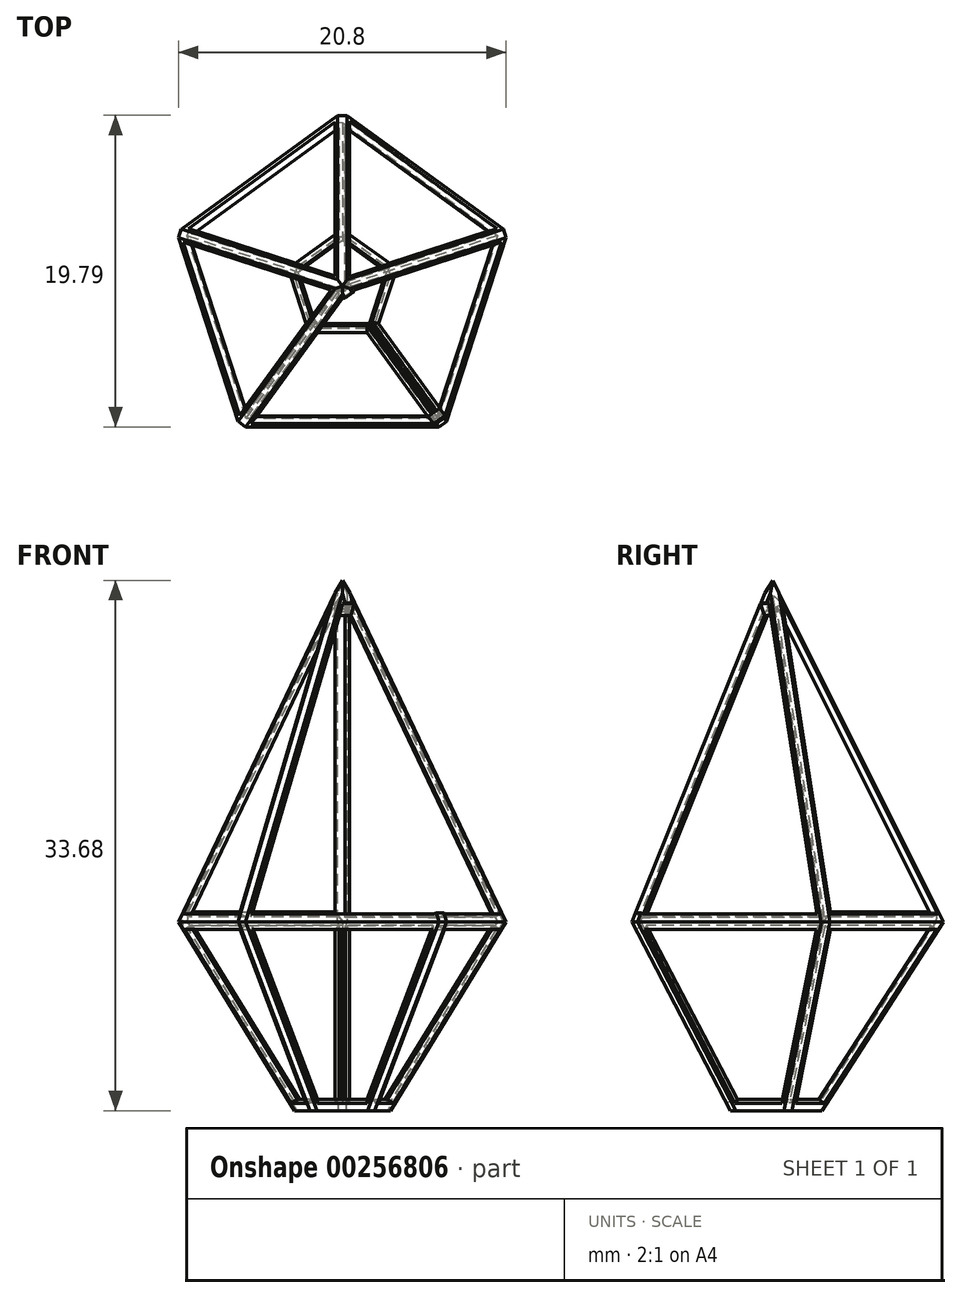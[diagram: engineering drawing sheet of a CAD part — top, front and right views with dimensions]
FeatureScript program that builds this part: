
annotation { "Feature Type Name" : "Feature", "Feature Type Description" : "" }
export const myFeature = defineFeature(function(context is Context, id is Id, definition is map)
    precondition{}
    {
        {
            var Q0;
            Q0=qCreatedBy(makeId("Top.planeOp"),FACE);
            var sketch = newSketch(context, id + "F0", { "sketchPlane" : qUnion([Q0])});
            skCircle(sketch, "E0.cCircle", {"center": v(0, 0) * mm, "radius": 8.94 * mm, "construction": true});
            skLineSegment(sketch, "E0.0", {"start": v(6.5, -8.94) * mm, "end": v(-6.5, -8.94) * mm});
            skLineSegment(sketch, "E0.1", {"start": v(-6.5, -8.94) * mm, "end": v(-10.51, 3.42) * mm});
            skLineSegment(sketch, "E0.2", {"start": v(-10.51, 3.42) * mm, "end": v(0, 11.06) * mm});
            skLineSegment(sketch, "E0.3", {"start": v(0, 11.06) * mm, "end": v(10.51, 3.42) * mm});
            skLineSegment(sketch, "E0.4", {"start": v(10.51, 3.42) * mm, "end": v(6.5, -8.94) * mm});
            skPoint(sketch, "E0.0.midPoint", {"position": v(0, -8.94) * mm});
            skSolve(sketch);
        }
        {
            var Q0;
            Q0=qCreatedBy(makeId("Top.planeOp"),FACE);
            cPlane(context, id + "F1", {"entities" : qUnion([Q0]), "cplaneType" : CPlaneType.OFFSET, "offset" : 22 * mm, "width" : 152.4 * mm, "height" : 152.4 * mm});
        }
        {
            var Q0;
            Q0=qCreatedBy(id+"F1.planeOp",FACE);
            var sketch = newSketch(context, id + "F2", { "sketchPlane" : qUnion([Q0])});
            skCircle(sketch, "E1.cCircle", {"center": v(0, 0) * mm, "radius": 0.04 * mm, "construction": true});
            skLineSegment(sketch, "E1.0", {"start": v(0.03, -0.04) * mm, "end": v(-0.03, -0.04) * mm});
            skLineSegment(sketch, "E1.1", {"start": v(-0.03, -0.04) * mm, "end": v(-0.05, 0.02) * mm});
            skLineSegment(sketch, "E1.2", {"start": v(-0.05, 0.02) * mm, "end": v(0, 0.06) * mm});
            skLineSegment(sketch, "E1.3", {"start": v(0, 0.06) * mm, "end": v(0.05, 0.02) * mm});
            skLineSegment(sketch, "E1.4", {"start": v(0.05, 0.02) * mm, "end": v(0.03, -0.04) * mm});
            skPoint(sketch, "E1.0.midPoint", {"position": v(0, -0.04) * mm});
            skSolve(sketch);
        }
        {
            var Q0;
            Q0=makeQuery(id+"F0.imprint","IMPRINT",FACE,{"disambiguationData":[TD([[makeQuery(id+"F0.imprint","IMPRINT",EDGE,{"derivedFrom":sQuery(id+"F0.wireOp",EDGE,"E0.0")}),-1.0]])]});
            var Q1;
            Q1=makeQuery(id+"F2.imprint","IMPRINT",FACE,{"disambiguationData":[TD([[makeQuery(id+"F2.imprint","IMPRINT",EDGE,{"derivedFrom":sQuery(id+"F2.wireOp",EDGE,"E1.0")}),-1.0]])]});
            loft(context, id + "F3", {"sheetProfilesArray" : [{ "sheetProfileEntities" : qUnion([Q0]) }, { "sheetProfileEntities" : qUnion([Q1]) }]});
        }
        {
            var Q0;
            Q0=qCreatedBy(makeId("Top.planeOp"),FACE);
            cPlane(context, id + "F4", {"entities" : qUnion([Q0]), "cplaneType" : CPlaneType.OFFSET, "offset" : 12 * mm, "oppositeDirection" : true, "width" : 150 * mm, "height" : 150 * mm});
        }
        {
            var Q0;
            Q0=qCreatedBy(id+"F4.planeOp",FACE);
            var sketch = newSketch(context, id + "F5", { "sketchPlane" : qUnion([Q0])});
            skCircle(sketch, "E2.cCircle", {"center": v(0, 0) * mm, "radius": 2.68 * mm, "construction": true});
            skLineSegment(sketch, "E2.0", {"start": v(1.95, -2.68) * mm, "end": v(-1.95, -2.68) * mm});
            skLineSegment(sketch, "E2.1", {"start": v(-1.95, -2.68) * mm, "end": v(-3.15, 1.02) * mm});
            skLineSegment(sketch, "E2.2", {"start": v(-3.15, 1.02) * mm, "end": v(0, 3.32) * mm});
            skLineSegment(sketch, "E2.3", {"start": v(0, 3.32) * mm, "end": v(3.15, 1.02) * mm});
            skLineSegment(sketch, "E2.4", {"start": v(3.15, 1.02) * mm, "end": v(1.95, -2.68) * mm});
            skPoint(sketch, "E2.0.midPoint", {"position": v(0, -2.68) * mm});
            skSolve(sketch);
        }
        {
            var Q1;
            Q1=makeQuery(id+"F3.opLoft","CAP_FACE",FACE,{"disambiguationData":[OSD([makeQuery(id+"F0.imprint","IMPRINT",FACE,{"disambiguationData":[TD([[makeQuery(id+"F0.imprint","IMPRINT",EDGE,{"derivedFrom":sQuery(id+"F0.wireOp",EDGE,"E0.0")}),-1.0]])]})])],"isStart":true});
            var Q2;
            Q2=makeQuery(id+"F5.imprint","IMPRINT",FACE,{"disambiguationData":[TD([[makeQuery(id+"F5.imprint","IMPRINT",EDGE,{"derivedFrom":sQuery(id+"F5.wireOp",EDGE,"E2.0")}),-1.0]])]});
            loft(context, id + "F6", {"operationType" : NewBodyOperationType.ADD, "sheetProfilesArray" : [{ "sheetProfileEntities" : qUnion([Q1]) }, { "sheetProfileEntities" : qUnion([Q2]) }]});
        }
        {
            var Q0;
            Q0=makeQuery(id+"F3.opLoft","SWEPT_FACE",FACE,{"disambiguationData":[OSD([sQuery(id+"F0.wireOp",EDGE,"E0.1"),sQuery(id+"F0.wireOp",EDGE,"E0.2"),sQuery(id+"F0.wireOp",EDGE,"E0.3"),sQuery(id+"F2.wireOp",EDGE,"E1.1"),sQuery(id+"F2.wireOp",EDGE,"E1.2"),sQuery(id+"F2.wireOp",EDGE,"E1.3")])]});
            shell(context, id + "F7", {"entities" : qUnion([Q0]), "thickness" : .5 * mm});
        }
        {
            var Q0;
            Q0=makeQuery(id+"F3.opLoft","SWEPT_FACE",FACE,{"disambiguationData":[OSD([sQuery(id+"F0.wireOp",EDGE,"E0.0"),sQuery(id+"F0.wireOp",EDGE,"E0.1"),sQuery(id+"F0.wireOp",EDGE,"E0.2"),sQuery(id+"F2.wireOp",EDGE,"E1.0"),sQuery(id+"F2.wireOp",EDGE,"E1.1"),sQuery(id+"F2.wireOp",EDGE,"E1.2")])]});
            var sketch = newSketch(context, id + "F8", { "sketchPlane" : qUnion([Q0])});
            skLineSegment(sketch, "E3", {"start": v(-5.4, -3.5) * mm, "end": v(6.1, -2.1) * mm});
            skLineSegment(sketch, "E4", {"start": v(6.1, -2.1) * mm, "end": v(-2.23, 18.31) * mm});
            skLineSegment(sketch, "E5", {"start": v(-2.23, 18.31) * mm, "end": v(-5.4, -3.5) * mm});
            skSolve(sketch);
        }
        {
            var Q0;
            Q0=makeQuery(id+"F3.opLoft","SWEPT_FACE",FACE,{"disambiguationData":[OSD([sQuery(id+"F0.wireOp",EDGE,"E0.0"),sQuery(id+"F0.wireOp",EDGE,"E0.1"),sQuery(id+"F0.wireOp",EDGE,"E0.4"),sQuery(id+"F2.wireOp",EDGE,"E1.0"),sQuery(id+"F2.wireOp",EDGE,"E1.1"),sQuery(id+"F2.wireOp",EDGE,"E1.4")])]});
            var sketch = newSketch(context, id + "F9", { "sketchPlane" : qUnion([Q0])});
            skLineSegment(sketch, "E6", {"start": v(-5.8, -2.81) * mm, "end": v(5.8, -2.81) * mm});
            skLineSegment(sketch, "E7", {"start": v(5.8, -2.81) * mm, "end": v(0, 18.44) * mm});
            skLineSegment(sketch, "E8", {"start": v(0, 18.44) * mm, "end": v(-5.8, -2.81) * mm});
            skSolve(sketch);
        }
        {
            var Q0;
            Q0=makeQuery(id+"F3.opLoft","SWEPT_FACE",FACE,{"disambiguationData":[OSD([sQuery(id+"F0.wireOp",EDGE,"E0.0"),sQuery(id+"F0.wireOp",EDGE,"E0.3"),sQuery(id+"F0.wireOp",EDGE,"E0.4"),sQuery(id+"F2.wireOp",EDGE,"E1.0"),sQuery(id+"F2.wireOp",EDGE,"E1.3"),sQuery(id+"F2.wireOp",EDGE,"E1.4")])]});
            var sketch = newSketch(context, id + "F10", { "sketchPlane" : qUnion([Q0])});
            skLineSegment(sketch, "E9", {"start": v(-6.09, -2.1) * mm, "end": v(5.4, -3.5) * mm});
            skLineSegment(sketch, "E10", {"start": v(5.4, -3.5) * mm, "end": v(2.23, 18.3) * mm});
            skLineSegment(sketch, "E11", {"start": v(2.23, 18.3) * mm, "end": v(-6.09, -2.1) * mm});
            skSolve(sketch);
        }
        {
            var Q0;
            Q0=makeQuery(id+"F3.opLoft","SWEPT_FACE",FACE,{"disambiguationData":[OSD([sQuery(id+"F0.wireOp",EDGE,"E0.2"),sQuery(id+"F0.wireOp",EDGE,"E0.3"),sQuery(id+"F0.wireOp",EDGE,"E0.4"),sQuery(id+"F2.wireOp",EDGE,"E1.2"),sQuery(id+"F2.wireOp",EDGE,"E1.3"),sQuery(id+"F2.wireOp",EDGE,"E1.4")])]});
            var sketch = newSketch(context, id + "F11", { "sketchPlane" : qUnion([Q0])});
            skLineSegment(sketch, "E12", {"start": v(-6.33, -1.2) * mm, "end": v(4.85, -4.24) * mm});
            skLineSegment(sketch, "E13", {"start": v(4.85, -4.24) * mm, "end": v(4.85, 17.8) * mm});
            skLineSegment(sketch, "E14", {"start": v(4.85, 17.8) * mm, "end": v(-6.33, -1.2) * mm});
            skSolve(sketch);
        }
        {
            var Q0;
            Q0=makeQuery(id+"F11.imprint","IMPRINT",FACE,{"disambiguationData":[TD([[makeQuery(id+"F11.imprint","IMPRINT",EDGE,{"derivedFrom":sQuery(id+"F11.wireOp",EDGE,"E12")}),1.0]])]});
            extrude(context, id + "F12", {"entities" : qUnion([Q0]), "operationType" : NewBodyOperationType.REMOVE, "oppositeDirection" : true, "depth" : 1 * mm});
        }
        {
            var Q0;
            Q0=makeQuery(id+"F10.imprint","IMPRINT",FACE,{"disambiguationData":[TD([[makeQuery(id+"F10.imprint","IMPRINT",EDGE,{"derivedFrom":sQuery(id+"F10.wireOp",EDGE,"E9")}),1.0]])]});
            extrude(context, id + "F13", {"entities" : qUnion([Q0]), "operationType" : NewBodyOperationType.REMOVE, "oppositeDirection" : true, "depth" : 1 * mm});
        }
        {
            var Q0;
            Q0=makeQuery(id+"F8.imprint","IMPRINT",FACE,{"disambiguationData":[TD([[makeQuery(id+"F8.imprint","IMPRINT",EDGE,{"derivedFrom":sQuery(id+"F8.wireOp",EDGE,"E3")}),1.0]])]});
            extrude(context, id + "F14", {"entities" : qUnion([Q0]), "operationType" : NewBodyOperationType.REMOVE, "oppositeDirection" : true, "depth" : 1 * mm});
        }
        {
            var Q0;
            Q0=makeQuery(id+"F9.imprint","IMPRINT",FACE,{"disambiguationData":[TD([[makeQuery(id+"F9.imprint","IMPRINT",EDGE,{"derivedFrom":sQuery(id+"F9.wireOp",EDGE,"E6")}),1.0]])]});
            extrude(context, id + "F15", {"entities" : qUnion([Q0]), "operationType" : NewBodyOperationType.REMOVE, "oppositeDirection" : true, "depth" : 1 * mm});
        }
        {
            var Q0;
            Q0=makeQuery(id+"F6.opLoft","SWEPT_FACE",FACE,{"disambiguationData":[OSD([sQuery(id+"F0.wireOp",EDGE,"E0.2"),sQuery(id+"F0.wireOp",EDGE,"E0.3"),sQuery(id+"F0.wireOp",EDGE,"E0.4"),sQuery(id+"F5.wireOp",EDGE,"E2.2"),sQuery(id+"F5.wireOp",EDGE,"E2.3"),sQuery(id+"F5.wireOp",EDGE,"E2.4")])]});
            var sketch = newSketch(context, id + "F16", { "sketchPlane" : qUnion([Q0])});
            skLineSegment(sketch, "E15", {"start": v(4.3, 5.24) * mm, "end": v(-6.6, 1.58) * mm});
            skLineSegment(sketch, "E16", {"start": v(-6.6, 1.58) * mm, "end": v(1.34, -8.9) * mm});
            skLineSegment(sketch, "E17", {"start": v(1.34, -8.9) * mm, "end": v(4.3, -7.9) * mm});
            skLineSegment(sketch, "E18", {"start": v(4.3, -7.9) * mm, "end": v(4.3, 5.24) * mm});
            skSolve(sketch);
        }
        {
            var Q0;
            Q0=makeQuery(id+"F6.opLoft","SWEPT_FACE",FACE,{"disambiguationData":[OSD([sQuery(id+"F0.wireOp",EDGE,"E0.1"),sQuery(id+"F0.wireOp",EDGE,"E0.2"),sQuery(id+"F0.wireOp",EDGE,"E0.3"),sQuery(id+"F5.wireOp",EDGE,"E2.1"),sQuery(id+"F5.wireOp",EDGE,"E2.2"),sQuery(id+"F5.wireOp",EDGE,"E2.3")])]});
            var sketch = newSketch(context, id + "F17", { "sketchPlane" : qUnion([Q0])});
            skLineSegment(sketch, "E19", {"start": v(6.6, 1.58) * mm, "end": v(-4.3, 5.24) * mm});
            skLineSegment(sketch, "E20", {"start": v(-4.3, 5.24) * mm, "end": v(-4.3, -7.9) * mm});
            skLineSegment(sketch, "E21", {"start": v(-1.34, -8.9) * mm, "end": v(-4.3, -7.9) * mm});
            skLineSegment(sketch, "E22", {"start": v(-1.34, -8.9) * mm, "end": v(6.6, 1.58) * mm});
            skSolve(sketch);
        }
        {
            var Q0;
            Q0=makeQuery(id+"F6.opLoft","SWEPT_FACE",FACE,{"disambiguationData":[OSD([sQuery(id+"F0.wireOp",EDGE,"E0.0"),sQuery(id+"F0.wireOp",EDGE,"E0.1"),sQuery(id+"F0.wireOp",EDGE,"E0.2"),sQuery(id+"F5.wireOp",EDGE,"E2.0"),sQuery(id+"F5.wireOp",EDGE,"E2.1"),sQuery(id+"F5.wireOp",EDGE,"E2.2")])]});
            var sketch = newSketch(context, id + "F18", { "sketchPlane" : qUnion([Q0])});
            skLineSegment(sketch, "E23", {"start": v(6.22, 2.7) * mm, "end": v(-5.15, 4.41) * mm});
            skLineSegment(sketch, "E24", {"start": v(-5.15, 4.41) * mm, "end": v(-2.86, -8.53) * mm});
            skLineSegment(sketch, "E25", {"start": v(0.23, -9) * mm, "end": v(-2.86, -8.53) * mm});
            skLineSegment(sketch, "E26", {"start": v(0.23, -9) * mm, "end": v(6.22, 2.7) * mm});
            skSolve(sketch);
        }
        {
            var Q0;
            Q0=makeQuery(id+"F6.opLoft","SWEPT_FACE",FACE,{"disambiguationData":[OSD([sQuery(id+"F0.wireOp",EDGE,"E0.0"),sQuery(id+"F0.wireOp",EDGE,"E0.1"),sQuery(id+"F0.wireOp",EDGE,"E0.4"),sQuery(id+"F5.wireOp",EDGE,"E2.0"),sQuery(id+"F5.wireOp",EDGE,"E2.1"),sQuery(id+"F5.wireOp",EDGE,"E2.4")])]});
            var sketch = newSketch(context, id + "F19", { "sketchPlane" : qUnion([Q0])});
            skLineSegment(sketch, "E27", {"start": v(5.75, 3.6) * mm, "end": v(-5.75, 3.6) * mm});
            skLineSegment(sketch, "E28", {"start": v(-5.75, 3.6) * mm, "end": v(-1.56, -8.86) * mm});
            skLineSegment(sketch, "E29", {"start": v(-1.56, -8.86) * mm, "end": v(1.56, -8.86) * mm});
            skLineSegment(sketch, "E30", {"start": v(1.56, -8.86) * mm, "end": v(5.75, 3.6) * mm});
            skSolve(sketch);
        }
        {
            var Q0;
            Q0=makeQuery(id+"F6.opLoft","SWEPT_FACE",FACE,{"disambiguationData":[OSD([sQuery(id+"F0.wireOp",EDGE,"E0.0"),sQuery(id+"F0.wireOp",EDGE,"E0.3"),sQuery(id+"F0.wireOp",EDGE,"E0.4"),sQuery(id+"F5.wireOp",EDGE,"E2.0"),sQuery(id+"F5.wireOp",EDGE,"E2.3"),sQuery(id+"F5.wireOp",EDGE,"E2.4")])]});
            var sketch = newSketch(context, id + "F20", { "sketchPlane" : qUnion([Q0])});
            skLineSegment(sketch, "E31", {"start": v(5.15, 4.41) * mm, "end": v(-6.22, 2.7) * mm});
            skLineSegment(sketch, "E32", {"start": v(-6.22, 2.7) * mm, "end": v(-0.23, -9) * mm});
            skLineSegment(sketch, "E33", {"start": v(-0.23, -9) * mm, "end": v(2.86, -8.53) * mm});
            skLineSegment(sketch, "E34", {"start": v(2.86, -8.53) * mm, "end": v(5.15, 4.41) * mm});
            skSolve(sketch);
        }
        {
            var Q0;
            Q0=makeQuery(id+"F20.imprint","IMPRINT",FACE,{"disambiguationData":[TD([[makeQuery(id+"F20.imprint","IMPRINT",EDGE,{"derivedFrom":sQuery(id+"F20.wireOp",EDGE,"E31")}),1.0]])]});
            extrude(context, id + "F21", {"entities" : qUnion([Q0]), "operationType" : NewBodyOperationType.REMOVE, "oppositeDirection" : true, "depth" : 1 * mm});
        }
        {
            var Q0;
            Q0=makeQuery(id+"F16.imprint","IMPRINT",FACE,{"disambiguationData":[TD([[makeQuery(id+"F16.imprint","IMPRINT",EDGE,{"derivedFrom":sQuery(id+"F16.wireOp",EDGE,"E15")}),1.0]])]});
            extrude(context, id + "F22", {"entities" : qUnion([Q0]), "operationType" : NewBodyOperationType.REMOVE, "oppositeDirection" : true, "depth" : 1 * mm});
        }
        {
            var Q0;
            Q0=makeQuery(id+"F19.imprint","IMPRINT",FACE,{"disambiguationData":[TD([[makeQuery(id+"F19.imprint","IMPRINT",EDGE,{"derivedFrom":sQuery(id+"F19.wireOp",EDGE,"E27")}),1.0]])]});
            extrude(context, id + "F23", {"entities" : qUnion([Q0]), "operationType" : NewBodyOperationType.REMOVE, "oppositeDirection" : true, "depth" : 1 * mm});
        }
        {
            var Q0;
            Q0=makeQuery(id+"F18.imprint","IMPRINT",FACE,{"disambiguationData":[TD([[makeQuery(id+"F18.imprint","IMPRINT",EDGE,{"derivedFrom":sQuery(id+"F18.wireOp",EDGE,"E23")}),1.0]])]});
            extrude(context, id + "F24", {"entities" : qUnion([Q0]), "operationType" : NewBodyOperationType.REMOVE, "oppositeDirection" : true, "depth" : 1 * mm});
        }
        {
            var Q0;
            Q0=makeQuery(id+"F17.imprint","IMPRINT",FACE,{"disambiguationData":[TD([[makeQuery(id+"F17.imprint","IMPRINT",EDGE,{"derivedFrom":sQuery(id+"F17.wireOp",EDGE,"E19")}),1.0]])]});
            extrude(context, id + "F25", {"entities" : qUnion([Q0]), "operationType" : NewBodyOperationType.REMOVE, "oppositeDirection" : true, "depth" : 1 * mm});
        }
        {
            var Q0;
            Q0=makeQuery(id+"F3.opLoft","SWEPT_EDGE",EDGE,{"disambiguationData":[OSD([sQuery(id+"F0.wireOp",EDGE,"E0.2"),sQuery(id+"F0.wireOp",EDGE,"E0.3"),sQuery(id+"F2.wireOp",EDGE,"E1.2"),sQuery(id+"F2.wireOp",EDGE,"E1.3")])]});
            var Q1;
            Q1=makeQuery(id+"F3.opLoft","SWEPT_EDGE",EDGE,{"disambiguationData":[OSD([sQuery(id+"F0.wireOp",EDGE,"E0.1"),sQuery(id+"F0.wireOp",EDGE,"E0.2"),sQuery(id+"F2.wireOp",EDGE,"E1.1"),sQuery(id+"F2.wireOp",EDGE,"E1.2")])]});
            var Q2;
            Q2=makeQuery(id+"F3.opLoft","SWEPT_EDGE",EDGE,{"disambiguationData":[OSD([sQuery(id+"F0.wireOp",EDGE,"E0.0"),sQuery(id+"F0.wireOp",EDGE,"E0.1"),sQuery(id+"F2.wireOp",EDGE,"E1.0"),sQuery(id+"F2.wireOp",EDGE,"E1.1")])]});
            var Q3;
            Q3=makeQuery(id+"F3.opLoft","SWEPT_EDGE",EDGE,{"disambiguationData":[OSD([sQuery(id+"F0.wireOp",EDGE,"E0.0"),sQuery(id+"F0.wireOp",EDGE,"E0.4"),sQuery(id+"F2.wireOp",EDGE,"E1.0"),sQuery(id+"F2.wireOp",EDGE,"E1.4")])]});
            var Q4;
            Q4=makeQuery(id+"F3.opLoft","SWEPT_EDGE",EDGE,{"disambiguationData":[OSD([sQuery(id+"F0.wireOp",EDGE,"E0.3"),sQuery(id+"F0.wireOp",EDGE,"E0.4"),sQuery(id+"F2.wireOp",EDGE,"E1.3"),sQuery(id+"F2.wireOp",EDGE,"E1.4")])]});
            chamfer(context, id + "F26", {"entities" : qUnion([Q0, Q1, Q2, Q3, Q4]), "width" : .54 * mm, "tangentPropagation" : true});
        }
        {
            var Q0;
            Q0=makeQuery(id+"F6.opLoft","SWEPT_EDGE",EDGE,{"disambiguationData":[OSD([sQuery(id+"F0.wireOp",EDGE,"E0.0"),sQuery(id+"F0.wireOp",EDGE,"E0.4"),sQuery(id+"F5.wireOp",EDGE,"E2.0"),sQuery(id+"F5.wireOp",EDGE,"E2.4")])]});
            var Q1;
            Q1=makeQuery(id+"F6.opLoft","SWEPT_EDGE",EDGE,{"disambiguationData":[OSD([sQuery(id+"F0.wireOp",EDGE,"E0.0"),sQuery(id+"F0.wireOp",EDGE,"E0.1"),sQuery(id+"F5.wireOp",EDGE,"E2.0"),sQuery(id+"F5.wireOp",EDGE,"E2.1")])]});
            var Q2;
            Q2=makeQuery(id+"F6.opLoft","SWEPT_EDGE",EDGE,{"disambiguationData":[OSD([sQuery(id+"F0.wireOp",EDGE,"E0.1"),sQuery(id+"F0.wireOp",EDGE,"E0.2"),sQuery(id+"F5.wireOp",EDGE,"E2.1"),sQuery(id+"F5.wireOp",EDGE,"E2.2")])]});
            var Q3;
            Q3=makeQuery(id+"F6.opLoft","SWEPT_EDGE",EDGE,{"disambiguationData":[OSD([sQuery(id+"F0.wireOp",EDGE,"E0.2"),sQuery(id+"F0.wireOp",EDGE,"E0.3"),sQuery(id+"F5.wireOp",EDGE,"E2.2"),sQuery(id+"F5.wireOp",EDGE,"E2.3")])]});
            var Q4;
            Q4=makeQuery(id+"F6.opLoft","SWEPT_EDGE",EDGE,{"disambiguationData":[OSD([sQuery(id+"F0.wireOp",EDGE,"E0.3"),sQuery(id+"F0.wireOp",EDGE,"E0.4"),sQuery(id+"F5.wireOp",EDGE,"E2.3"),sQuery(id+"F5.wireOp",EDGE,"E2.4")])]});
            chamfer(context, id + "F27", {"entities" : qUnion([Q0, Q1, Q2, Q3, Q4]), "width" : .54 * mm, "tangentPropagation" : true});
        }
        {
            var Q0;
            Q0=makeQuery(id+"F26.opChamfer","BLEND_FACE",FACE,{"disambiguationData":[OSD([sQuery(id+"F0.wireOp",EDGE,"E0.0"),sQuery(id+"F0.wireOp",EDGE,"E0.4"),sQuery(id+"F2.wireOp",EDGE,"E1.0"),sQuery(id+"F2.wireOp",EDGE,"E1.4")])]});
            var sketch = newSketch(context, id + "F28", { "sketchPlane" : qUnion([Q0])});
            skLineSegment(sketch, "E35", {"start": v(0.88, -4.17) * mm, "end": v(1.74, -3.9) * mm});
            skLineSegment(sketch, "E36", {"start": v(1.74, -3.9) * mm, "end": v(-5.07, 17.06) * mm});
            skLineSegment(sketch, "E37", {"start": v(-5.07, 17.06) * mm, "end": v(-5.93, 16.78) * mm});
            skLineSegment(sketch, "E38", {"start": v(-5.93, 16.78) * mm, "end": v(0.88, -4.17) * mm});
            skSolve(sketch);
        }
        {
            var Q0;
            Q0=makeQuery(id+"F28.imprint","IMPRINT",FACE,{"disambiguationData":[TD([[makeQuery(id+"F28.imprint","IMPRINT",EDGE,{"derivedFrom":sQuery(id+"F28.wireOp",EDGE,"E35")}),1.0]])]});
            extrude(context, id + "F29", {"entities" : qUnion([Q0]), "operationType" : NewBodyOperationType.REMOVE, "oppositeDirection" : true, "depth" : 1 * mm});
        }
        {
            var Q0;
            Q0=makeQuery(id+"F29.boolean.opBoolean","COPY",FACE,{"disambiguationData":[TD([makeQuery(id+"F15.boolean.opBoolean","COPY",FACE,{"derivedFrom":makeQuery(id+"F15.opExtrude","SWEPT_FACE",FACE,{"disambiguationData":[OSD([sQuery(id+"F9.wireOp",EDGE,"E6")])]})})])],"derivedFrom":makeQuery(id+"F29.opExtrude","SWEPT_FACE",FACE,{"disambiguationData":[OSD([sQuery(id+"F28.wireOp",EDGE,"E38")])]})});
            extrude(context, id + "F30", {"entities" : qUnion([Q0]), "operationType" : NewBodyOperationType.ADD, "depth" : 0.91 * mm});
        }
        {
            var Q0;
            Q0=makeQuery(id+"F29.boolean.opBoolean","COPY",FACE,{"disambiguationData":[TD([makeQuery(id+"F14.boolean.opBoolean","COPY",FACE,{"derivedFrom":makeQuery(id+"F14.opExtrude","SWEPT_FACE",FACE,{"disambiguationData":[OSD([sQuery(id+"F8.wireOp",EDGE,"E4")])]})})])],"derivedFrom":makeQuery(id+"F29.opExtrude","SWEPT_FACE",FACE,{"disambiguationData":[OSD([sQuery(id+"F28.wireOp",EDGE,"E38")])]})});
            extrude(context, id + "F31", {"entities" : qUnion([Q0]), "operationType" : NewBodyOperationType.ADD, "depth" : 0.9 * mm});
        }
    });
